# Revit family: Дверь входная с открыванием на улицу
name_source: partatom
category: Двери
revit_build: Autodesk Revit 2016 (Build: 20160314_0715(x64)
units: mm (PartAtom-declared; Revit-internal decimal feet)

## family parameters
Всегда вертикально = Да
Заголовок OmniClass = Doors
Номер OmniClass = 23.30.10.00
Общий = Нет
Основа = Стена
При загрузке вырезать с полостями = Нет
Точка расчета площади = Нет

## types (2) — shared parameters
ADSK_URL документации изделия = https://store.brusbox.ru
ADSK_Версия Revit = Autodesk Revit 2016
ADSK_Единица измерения = шт
ADSK_Завод-изготовитель = ООО "БРУСБОКС"
BL_BIM library = https://bimlib.ru
Rед = 1.0000 (м²·K)/Вт
URL = https://brusbox.ru
λ_КраевойЗоныСтеклопакета = 0.0600 (м²·K)/Вт
Аналитическая конструкция = <Нет>
Замыкание стены = По основе
ЗубСтворки_Высота = 20 мм
Изготовитель = ООО "БРУСБОКС"
КлассПожарнойОпасности = КМ3
Порог_Материал = АС_Металл_Алюминий
Профиль_Материал = <По категории>
Рама_ВысотаПрофиля = 64 мм
РасчетноеЗначениеВетровойНагрузки = 400
Створка_ВысотаПрофиля = 78 мм
Стеклопакет_Материал = Стекло
Сэндвич_Материал = <По категории>
Сэндвич_Толщина = 32 мм
ТехническиеУсловия_или_ГОСТ = ГОСТ 30673-2013, ГОСТ-24866-2014, ГОСТ-30674-99, ГОСТ 30971-2012
Функция = Наружные слои
zero-valued in all types: Высота, Выступ каркаса внут., Выступ каркаса нар., Примерная высота, Примерная ширина, Толщина, Ширина, Ширина каркаса

## per-type parameters (varying)
| type | ADSK_Наименование краткое | Rпрофиля | Rстеклопакета | АлюминиевыйПорог_Ширина | АртикулРамы_АрмированияРамы | АртикулСтворки_АрмированияСтворки | ЗубСтворки_Ширина | КлассСопротивленияТеплопередаче | Порог_Артикул | ПрофильнаяСистема_Наименование | Рама_ШиринаПрофиля | Смещение | Створка_ШиринаПрофиля | Стеклопакет_Толщина | Стеклопакет_Формула |
| Дверь входная Т118 60 мм с открыванием на улицу | Дверь Т118-60 | 0.7300 (м²·K)/Вт | 0.7500 (м²·K)/Вт | 58 мм | 10201064/40108020 | 10302118/40108028 | 14 мм | Б1 (порог - рама ПВХ) | 40301017 | Дверная система BRUSBOX 60 | 60 мм | 18 мм | 60 мм | 32 мм | 4-10-4-10-4И |
| Дверь входная Т118 70 мм с открыванием на улицу | Дверь Т118-70 | 0.9300 (м²·K)/Вт | 0.9300 (м²·K)/Вт | 68 мм | 10401064/40108020 | 10702118/40108028 | 16 мм | А1 (порог - рама ПВХ) | 40701017 | Дверная система BRUSBOX 70 | 70 мм | 20 мм | 70 мм | 40 мм | 4И-10-4-10И |

note: column(s) folded — value = type name in every type: Наименование

## geometry (parser evidence)
native form markers: Blend x14
no freeform markers — native parametric forms only
